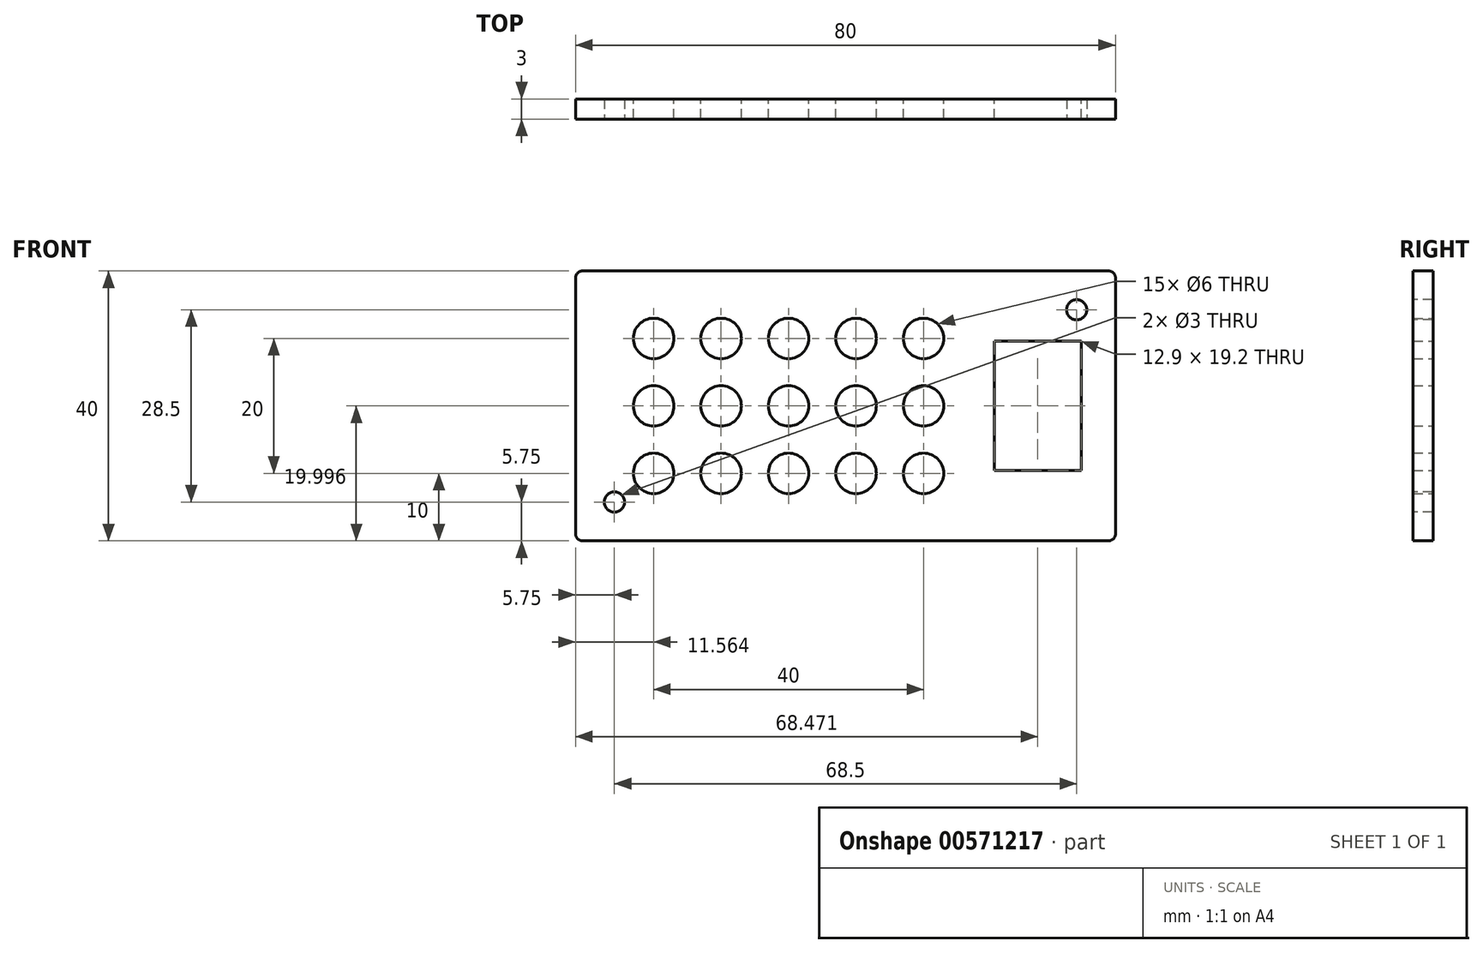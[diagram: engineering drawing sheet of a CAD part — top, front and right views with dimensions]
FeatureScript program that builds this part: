
annotation { "Feature Type Name" : "Feature", "Feature Type Description" : "" }
export const myFeature = defineFeature(function(context is Context, id is Id, definition is map)
    precondition{}
    {
        {
            var Q0;
            Q0=qCreatedBy(makeId("Front.planeOp"),FACE);
            var sketch = newSketch(context, id + "F0", { "sketchPlane" : qUnion([Q0])});
            skLineSegment(sketch, "E0.bottom", {"start": v(-40, 20) * mm, "end": v(40, 20) * mm});
            skLineSegment(sketch, "E0.top", {"start": v(-40, -20) * mm, "end": v(40, -20) * mm});
            skLineSegment(sketch, "E0.left", {"start": v(-40, 20) * mm, "end": v(-40, -20) * mm});
            skLineSegment(sketch, "E0.right", {"start": v(40, 20) * mm, "end": v(40, -20) * mm});
            skLineSegment(sketch, "E1", {"start": v(-40, 20) * mm, "end": v(40, -20) * mm, "construction": true});
            skSolve(sketch);
        }
        {
            var Q0;
            Q0=makeQuery(id+"F0.imprint","IMPRINT",FACE,{"disambiguationData":[TD([[makeQuery(id+"F0.imprint","IMPRINT",EDGE,{"derivedFrom":sQuery(id+"F0.wireOp",EDGE,"E0.bottom")}),-1.0]])]});
            var sketch = newSketch(context, id + "F1", { "sketchPlane" : qUnion([Q0])});
            skCircle(sketch, "E2", {"center": v(-28.44, 10) * mm, "radius": 3 * mm});
            skCircle(sketch, "E3.0.1.0", {"center": v(-28.44, 0) * mm, "radius": 3 * mm});
            skCircle(sketch, "E3.0.2.0", {"center": v(-28.44, -10) * mm, "radius": 3 * mm});
            skCircle(sketch, "E3.1.0.0", {"center": v(-18.44, 10) * mm, "radius": 3 * mm});
            skCircle(sketch, "E3.1.1.0", {"center": v(-18.44, 0) * mm, "radius": 3 * mm});
            skCircle(sketch, "E3.1.2.0", {"center": v(-18.44, -10) * mm, "radius": 3 * mm});
            skCircle(sketch, "E3.2.0.0", {"center": v(-8.44, 10) * mm, "radius": 3 * mm});
            skCircle(sketch, "E3.2.1.0", {"center": v(-8.44, 0) * mm, "radius": 3 * mm});
            skCircle(sketch, "E3.2.2.0", {"center": v(-8.44, -10) * mm, "radius": 3 * mm});
            skCircle(sketch, "E3.3.0.0", {"center": v(1.56, 10) * mm, "radius": 3 * mm});
            skCircle(sketch, "E3.3.1.0", {"center": v(1.56, 0) * mm, "radius": 3 * mm});
            skCircle(sketch, "E3.3.2.0", {"center": v(1.56, -10) * mm, "radius": 3 * mm});
            skCircle(sketch, "E3.4.0.0", {"center": v(11.56, 10) * mm, "radius": 3 * mm});
            skCircle(sketch, "E3.4.1.0", {"center": v(11.56, 0) * mm, "radius": 3 * mm});
            skCircle(sketch, "E3.4.2.0", {"center": v(11.56, -10) * mm, "radius": 3 * mm});
            skLineSegment(sketch, "E3.direction1", {"start": v(-28.44, 10) * mm, "end": v(-18.44, 10) * mm, "construction": true});
            skLineSegment(sketch, "E3.direction2", {"start": v(-28.44, 10) * mm, "end": v(-28.44, 0) * mm, "construction": true});
            skLineSegment(sketch, "E4.bottom", {"start": v(22.02, 9.6) * mm, "end": v(34.92, 9.6) * mm});
            skLineSegment(sketch, "E4.top", {"start": v(22.02, -9.6) * mm, "end": v(34.92, -9.6) * mm});
            skLineSegment(sketch, "E4.left", {"start": v(22.02, 9.6) * mm, "end": v(22.02, -9.6) * mm});
            skLineSegment(sketch, "E4.right", {"start": v(34.92, 9.6) * mm, "end": v(34.92, -9.6) * mm});
            skLineSegment(sketch, "E5", {"start": v(22.02, 0) * mm, "end": v(34.92, 0) * mm, "construction": true});
            skLineSegment(sketch, "E6", {"start": v(11.56, 0) * mm, "end": v(1.56, 0) * mm, "construction": true});
            skSolve(sketch);
        }
        {
            var Q0;
            Q0 = qSketchRegion(id + "F0", true);
            extrude(context, id + "F2", {"entities" : qUnion([Q0]), "depth" : 3 * mm, "offsetDistance" : 25 * mm});
        }
        {
            var Q0;
            Q0 = qSketchRegion(id + "F1", true);
            extrude(context, id + "F3", {"entities" : qUnion([Q0]), "operationType" : NewBodyOperationType.REMOVE, "endBound" : BoundingType.THROUGH_ALL, "depth" : 25 * mm, "offsetDistance" : 25 * mm});
        }
        {
            var Q0;
            Q0=makeQuery(id+"F2.opExtrude","SWEPT_EDGE",EDGE,{"disambiguationData":[OSD([sQuery(id+"F0.wireOp",EDGE,"E0.bottom"),sQuery(id+"F0.wireOp",EDGE,"E0.left")])]});
            var Q1;
            Q1=makeQuery(id+"F2.opExtrude","SWEPT_EDGE",EDGE,{"disambiguationData":[OSD([sQuery(id+"F0.wireOp",EDGE,"E0.bottom"),sQuery(id+"F0.wireOp",EDGE,"E0.right")])]});
            var Q2;
            Q2=makeQuery(id+"F2.opExtrude","SWEPT_EDGE",EDGE,{"disambiguationData":[OSD([sQuery(id+"F0.wireOp",EDGE,"E0.top"),sQuery(id+"F0.wireOp",EDGE,"E0.right")])]});
            var Q3;
            Q3=makeQuery(id+"F2.opExtrude","SWEPT_EDGE",EDGE,{"disambiguationData":[OSD([sQuery(id+"F0.wireOp",EDGE,"E0.top"),sQuery(id+"F0.wireOp",EDGE,"E0.left")])]});
            fillet(context, id + "F4", {"entities" : qUnion([Q0, Q1, Q2, Q3]), "radius" : 1 * mm, "tangentPropagation" : true, "allowEdgeOverflow" : false});
        }
        {
            var Q0;
            Q0=makeQuery(id+"F2.opExtrude","CAP_FACE",FACE,{"disambiguationData":[OSD([sQuery(id+"F0.wireOp",EDGE,"E0.bottom"),sQuery(id+"F0.wireOp",EDGE,"E0.top"),sQuery(id+"F0.wireOp",EDGE,"E0.left"),sQuery(id+"F0.wireOp",EDGE,"E0.right")])],"isStart":false});
            var sketch = newSketch(context, id + "F5", { "sketchPlane" : qUnion([Q0])});
            skCircle(sketch, "E7", {"center": v(34.25, 14.25) * mm, "radius": 1.5 * mm});
            skCircle(sketch, "E8", {"center": v(-34.25, -14.25) * mm, "radius": 1.5 * mm});
            skLineSegment(sketch, "E9", {"start": v(-34.25, -14.25) * mm, "end": v(34.25, 14.25) * mm, "construction": true});
            skSolve(sketch);
        }
        {
            var Q0;
            Q0 = qSketchRegion(id + "F5", true);
            extrude(context, id + "F6", {"entities" : qUnion([Q0]), "operationType" : NewBodyOperationType.REMOVE, "oppositeDirection" : true, "depth" : 25 * mm, "offsetDistance" : 25 * mm});
        }
    });
